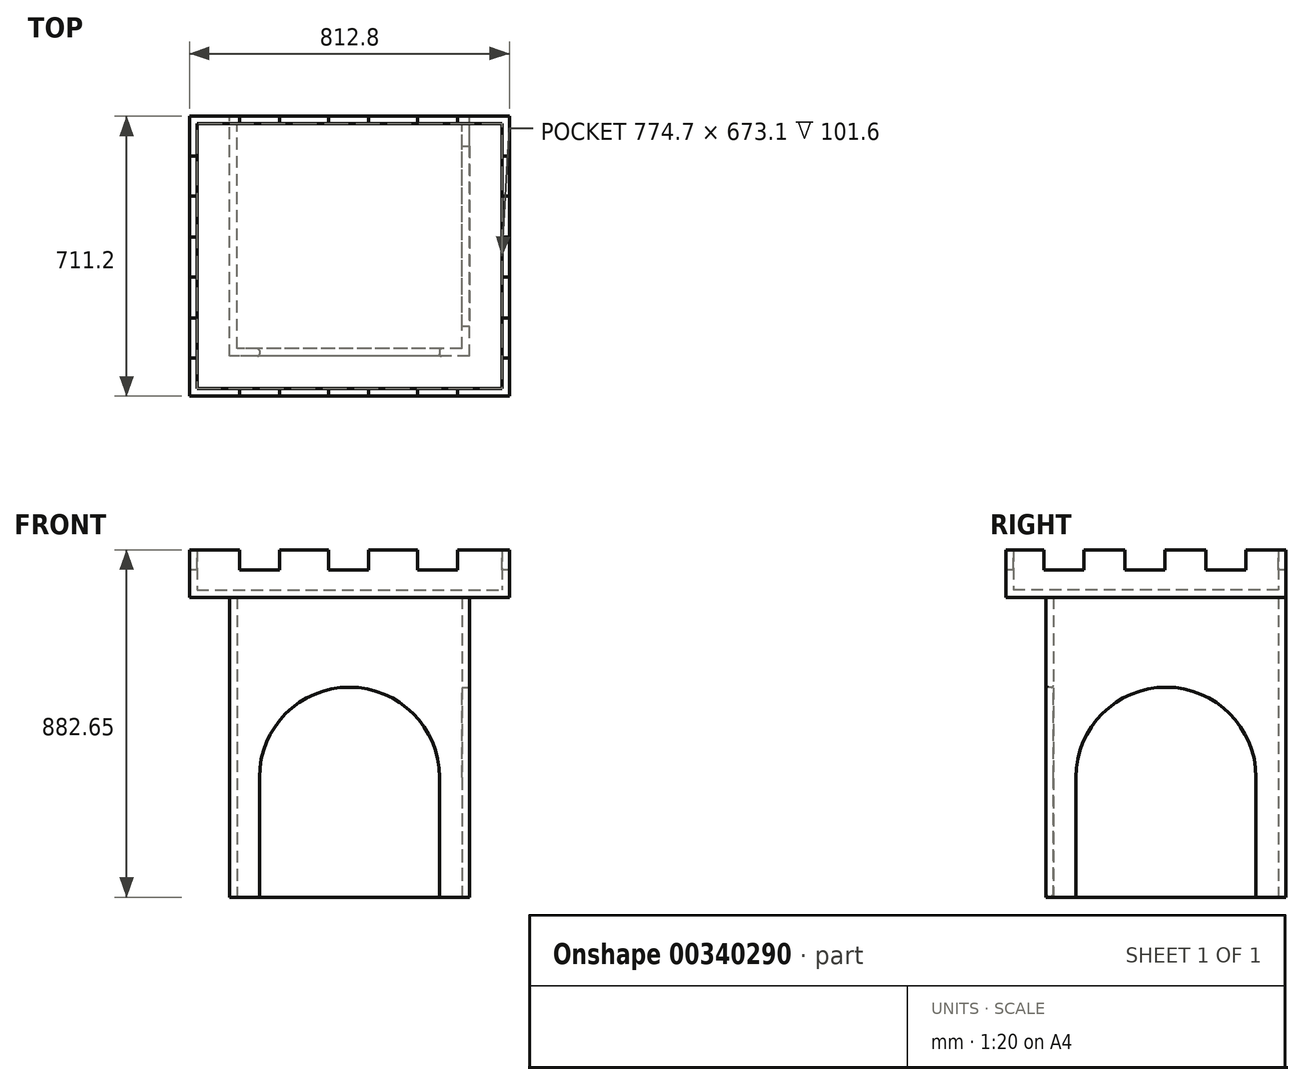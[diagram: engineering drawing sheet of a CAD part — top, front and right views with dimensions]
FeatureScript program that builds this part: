
annotation { "Feature Type Name" : "Feature", "Feature Type Description" : "" }
export const myFeature = defineFeature(function(context is Context, id is Id, definition is map)
    precondition{}
    {
        {
            var Q0;
            Q0=qCreatedBy(makeId("Top.planeOp"),FACE);
            var sketch = newSketch(context, id + "F0", { "sketchPlane" : qUnion([Q0])});
            skLineSegment(sketch, "E0.bottom", {"start": v(304.8, -304.8) * mm, "end": v(-304.8, -304.8) * mm});
            skLineSegment(sketch, "E0.top", {"start": v(304.8, 304.8) * mm, "end": v(-304.8, 304.8) * mm});
            skLineSegment(sketch, "E0.left", {"start": v(304.8, -304.8) * mm, "end": v(304.8, 304.8) * mm});
            skLineSegment(sketch, "E0.right", {"start": v(-304.8, -304.8) * mm, "end": v(-304.8, 304.8) * mm});
            skPoint(sketch, "E0.middle", {"position": v(0, 0) * mm});
            skLineSegment(sketch, "E1.bottom", {"start": v(285.75, -285.75) * mm, "end": v(-285.75, -285.75) * mm});
            skLineSegment(sketch, "E1.top", {"start": v(285.75, 285.75) * mm, "end": v(-285.75, 285.75) * mm});
            skLineSegment(sketch, "E1.left", {"start": v(285.75, -285.75) * mm, "end": v(285.75, 285.75) * mm});
            skLineSegment(sketch, "E1.right", {"start": v(-285.75, -285.75) * mm, "end": v(-285.75, 285.75) * mm});
            skSolve(sketch);
        }
        {
            var Q0;
            Q0 = qSketchRegion(id + "F0", true);
            extrude(context, id + "F1", {"entities" : qUnion([Q0]), "endBound" : BoundingType.SYMMETRIC, "depth" : 762 * mm});
        }
        {
            var Q0;
            Q0=makeQuery(id+"F1.opExtrude","SWEPT_FACE",FACE,{"disambiguationData":[OSD([sQuery(id+"F0.wireOp",EDGE,"E0.bottom")])]});
            var sketch = newSketch(context, id + "F2", { "sketchPlane" : qUnion([Q0])});
            skLineSegment(sketch, "E2.bottom", {"start": v(-228.6, -381) * mm, "end": v(228.6, -381) * mm});
            skLineSegment(sketch, "E2.top", {"start": v(-228.6, -76.2) * mm, "end": v(228.6, -76.2) * mm, "construction": true});
            skLineSegment(sketch, "E2.left", {"start": v(-228.6, -381) * mm, "end": v(-228.6, -76.2) * mm});
            skLineSegment(sketch, "E2.right", {"start": v(228.6, -381) * mm, "end": v(228.6, -76.2) * mm});
            skLineSegment(sketch, "E3", {"start": v(-304.8, -381) * mm, "end": v(-228.6, -381) * mm, "construction": true});
            skLineSegment(sketch, "E4", {"start": v(228.6, -381) * mm, "end": v(304.8, -381) * mm, "construction": true});
            skArc(sketch, "E5", {"start": v(228.6, -76.2) * mm, "mid": v(0, 152.4) * mm, "end": v(-228.6, -76.2) * mm});
            skSolve(sketch);
        }
        {
            var Q0;
            Q0 = qSketchRegion(id + "F2", true);
            extrude(context, id + "F3", {"entities" : qUnion([Q0]), "operationType" : NewBodyOperationType.REMOVE, "oppositeDirection" : true, "depth" : 25.4 * mm});
        }
        {
            var Q0;
            Q0=makeQuery(id+"F1.opExtrude","SWEPT_FACE",FACE,{"disambiguationData":[OSD([sQuery(id+"F0.wireOp",EDGE,"E0.left")])]});
            var sketch = newSketch(context, id + "F4", { "sketchPlane" : qUnion([Q0])});
            skLineSegment(sketch, "E6.bottom", {"start": v(-228.6, -381) * mm, "end": v(228.6, -381) * mm});
            skLineSegment(sketch, "E6.top", {"start": v(-228.6, -76.2) * mm, "end": v(228.6, -76.2) * mm, "construction": true});
            skLineSegment(sketch, "E6.left", {"start": v(-228.6, -381) * mm, "end": v(-228.6, -76.2) * mm});
            skLineSegment(sketch, "E6.right", {"start": v(228.6, -381) * mm, "end": v(228.6, -76.2) * mm});
            skLineSegment(sketch, "E7", {"start": v(-228.6, -381) * mm, "end": v(-304.8, -381) * mm, "construction": true});
            skLineSegment(sketch, "E8", {"start": v(228.6, -381) * mm, "end": v(304.8, -381) * mm, "construction": true});
            skArc(sketch, "E9", {"start": v(228.6, -76.2) * mm, "mid": v(0, 152.4) * mm, "end": v(-228.6, -76.2) * mm});
            skSolve(sketch);
        }
        {
            var Q0;
            Q0 = qSketchRegion(id + "F4", true);
            extrude(context, id + "F5", {"entities" : qUnion([Q0]), "operationType" : NewBodyOperationType.REMOVE, "oppositeDirection" : true, "depth" : 25.4 * mm});
        }
        {
            var Q0;
            Q0=makeQuery(id+"F3.boolean.opBoolean","COPY",FACE,{"derivedFrom":makeQuery(id+"F3.opExtrude","SWEPT_FACE",FACE,{"disambiguationData":[OSD([sQuery(id+"F2.wireOp",EDGE,"E2.left")])]})});
            var Q1;
            Q1=makeQuery(id+"F3.boolean.opBoolean","COPY",FACE,{"derivedFrom":makeQuery(id+"F3.opExtrude","SWEPT_FACE",FACE,{"disambiguationData":[OSD([sQuery(id+"F2.wireOp",EDGE,"E5")])]})});
            var Q2;
            Q2=makeQuery(id+"F3.boolean.opBoolean","COPY",FACE,{"derivedFrom":makeQuery(id+"F3.opExtrude","SWEPT_FACE",FACE,{"disambiguationData":[OSD([sQuery(id+"F2.wireOp",EDGE,"E2.right")])]})});
            fillet(context, id + "F6", {"entities" : qUnion([Q0, Q1, Q2]), "radius" : 5.08 * mm, "tangentPropagation" : true, "allowEdgeOverflow" : false});
        }
        {
            var Q0;
            Q0=makeQuery(id+"F1.opExtrude","CAP_FACE",FACE,{"disambiguationData":[OSD([sQuery(id+"F0.wireOp",EDGE,"E0.bottom"),sQuery(id+"F0.wireOp",EDGE,"E0.top"),sQuery(id+"F0.wireOp",EDGE,"E0.left"),sQuery(id+"F0.wireOp",EDGE,"E0.right"),sQuery(id+"F0.wireOp",EDGE,"E1.bottom"),sQuery(id+"F0.wireOp",EDGE,"E1.top"),sQuery(id+"F0.wireOp",EDGE,"E1.left"),sQuery(id+"F0.wireOp",EDGE,"E1.right")])],"isStart":false});
            var sketch = newSketch(context, id + "F7", { "sketchPlane" : qUnion([Q0])});
            skLineSegment(sketch, "E10.bottom", {"start": v(-406.4, 304.8) * mm, "end": v(406.4, 304.8) * mm});
            skLineSegment(sketch, "E10.top", {"start": v(-406.4, -406.4) * mm, "end": v(406.4, -406.4) * mm});
            skLineSegment(sketch, "E10.left", {"start": v(-406.4, 304.8) * mm, "end": v(-406.4, -406.4) * mm});
            skLineSegment(sketch, "E10.right", {"start": v(406.4, 304.8) * mm, "end": v(406.4, -406.4) * mm});
            skPoint(sketch, "E11", {"position": v(0, 304.8) * mm});
            skSolve(sketch);
        }
        {
            var Q0;
            Q0 = qSketchRegion(id + "F7", true);
            extrude(context, id + "F8", {"entities" : qUnion([Q0]), "operationType" : NewBodyOperationType.ADD, "depth" : 19.05 * mm});
        }
        {
            var Q0;
            Q0=makeQuery(id+"F8.opExtrude","CAP_FACE",FACE,{"disambiguationData":[OSD([sQuery(id+"F7.wireOp",EDGE,"E10.bottom"),sQuery(id+"F7.wireOp",EDGE,"E10.top"),sQuery(id+"F7.wireOp",EDGE,"E10.left"),sQuery(id+"F7.wireOp",EDGE,"E10.right")])],"isStart":false});
            var sketch = newSketch(context, id + "F9", { "sketchPlane" : qUnion([Q0])});
            skLineSegment(sketch, "E12.bottom", {"start": v(-406.4, 304.8) * mm, "end": v(406.4, 304.8) * mm});
            skLineSegment(sketch, "E12.top", {"start": v(-406.4, -406.4) * mm, "end": v(406.4, -406.4) * mm});
            skLineSegment(sketch, "E12.left", {"start": v(-406.4, 304.8) * mm, "end": v(-406.4, -406.4) * mm});
            skLineSegment(sketch, "E12.right", {"start": v(406.4, 304.8) * mm, "end": v(406.4, -406.4) * mm});
            skLineSegment(sketch, "E13.bottom", {"start": v(-387.35, 285.75) * mm, "end": v(387.35, 285.75) * mm});
            skLineSegment(sketch, "E13.top", {"start": v(-387.35, -387.35) * mm, "end": v(387.35, -387.35) * mm});
            skLineSegment(sketch, "E13.left", {"start": v(-387.35, 285.75) * mm, "end": v(-387.35, -387.35) * mm});
            skLineSegment(sketch, "E13.right", {"start": v(387.35, 285.75) * mm, "end": v(387.35, -387.35) * mm});
            skSolve(sketch);
        }
        {
            var Q0;
            Q0 = qSketchRegion(id + "F9", true);
            extrude(context, id + "F10", {"entities" : qUnion([Q0]), "operationType" : NewBodyOperationType.ADD, "depth" : 101.6 * mm});
        }
        {
            var Q0;
            Q0=makeQuery(id+"F10.boolean.opBoolean","MERGE",FACE,{"derivedFrom":[makeQuery(id+"F8.opExtrude","SWEPT_FACE",FACE,{"disambiguationData":[OSD([sQuery(id+"F7.wireOp",EDGE,"E10.top")])]}),makeQuery(id+"F10.opExtrude","SWEPT_FACE",FACE,{"disambiguationData":[OSD([sQuery(id+"F9.wireOp",EDGE,"E12.top")])]})]});
            var sketch = newSketch(context, id + "F11", { "sketchPlane" : qUnion([Q0])});
            skLineSegment(sketch, "E14", {"start": v(-406.4, 501.65) * mm, "end": v(-279.4, 501.65) * mm, "construction": true});
            skLineSegment(sketch, "E15.bottom", {"start": v(-279.4, 501.65) * mm, "end": v(-177.8, 501.65) * mm});
            skLineSegment(sketch, "E15.top", {"start": v(-279.4, 450.85) * mm, "end": v(-177.8, 450.85) * mm});
            skLineSegment(sketch, "E15.left", {"start": v(-279.4, 501.65) * mm, "end": v(-279.4, 450.85) * mm});
            skLineSegment(sketch, "E15.right", {"start": v(-177.8, 501.65) * mm, "end": v(-177.8, 450.85) * mm});
            skLineSegment(sketch, "E16.1.0.0", {"start": v(-180.34, 501.65) * mm, "end": v(-53.34, 501.65) * mm, "construction": true});
            skLineSegment(sketch, "E16.1.0.1", {"start": v(-53.34, 501.65) * mm, "end": v(48.26, 501.65) * mm});
            skLineSegment(sketch, "E16.1.0.2", {"start": v(-53.34, 450.85) * mm, "end": v(48.26, 450.85) * mm});
            skLineSegment(sketch, "E16.1.0.3", {"start": v(-53.34, 501.65) * mm, "end": v(-53.34, 450.85) * mm});
            skLineSegment(sketch, "E16.1.0.4", {"start": v(48.26, 501.65) * mm, "end": v(48.26, 450.85) * mm});
            skLineSegment(sketch, "E16.2.0.0", {"start": v(45.72, 501.65) * mm, "end": v(172.72, 501.65) * mm, "construction": true});
            skLineSegment(sketch, "E16.2.0.1", {"start": v(172.72, 501.65) * mm, "end": v(274.32, 501.65) * mm});
            skLineSegment(sketch, "E16.2.0.2", {"start": v(172.72, 450.85) * mm, "end": v(274.32, 450.85) * mm});
            skLineSegment(sketch, "E16.2.0.3", {"start": v(172.72, 501.65) * mm, "end": v(172.72, 450.85) * mm});
            skLineSegment(sketch, "E16.2.0.4", {"start": v(274.32, 501.65) * mm, "end": v(274.32, 450.85) * mm});
            skLineSegment(sketch, "E16.direction1", {"start": v(-406.4, 501.65) * mm, "end": v(-180.34, 501.65) * mm, "construction": true});
            skSolve(sketch);
        }
        {
            var Q0;
            Q0 = qSketchRegion(id + "F11", true);
            extrude(context, id + "F12", {"entities" : qUnion([Q0]), "operationType" : NewBodyOperationType.REMOVE, "endBound" : BoundingType.THROUGH_ALL, "oppositeDirection" : true, "depth" : 25.4 * mm});
        }
        {
            var Q0;
            Q0=makeQuery(id+"F10.boolean.opBoolean","MERGE",FACE,{"derivedFrom":[makeQuery(id+"F8.opExtrude","SWEPT_FACE",FACE,{"disambiguationData":[OSD([sQuery(id+"F7.wireOp",EDGE,"E10.left")])]}),makeQuery(id+"F10.opExtrude","SWEPT_FACE",FACE,{"disambiguationData":[OSD([sQuery(id+"F9.wireOp",EDGE,"E12.left")])]})]});
            var sketch = newSketch(context, id + "F13", { "sketchPlane" : qUnion([Q0])});
            skLineSegment(sketch, "E17", {"start": v(-304.8, 501.65) * mm, "end": v(-203.2, 501.65) * mm, "construction": true});
            skLineSegment(sketch, "E18.bottom", {"start": v(-203.2, 501.65) * mm, "end": v(-101.6, 501.65) * mm});
            skLineSegment(sketch, "E18.top", {"start": v(-203.2, 450.85) * mm, "end": v(-101.6, 450.85) * mm});
            skLineSegment(sketch, "E18.left", {"start": v(-203.2, 501.65) * mm, "end": v(-203.2, 450.85) * mm});
            skLineSegment(sketch, "E18.right", {"start": v(-101.6, 501.65) * mm, "end": v(-101.6, 450.85) * mm});
            skLineSegment(sketch, "E19.1.0.0", {"start": v(-99.06, 501.65) * mm, "end": v(2.54, 501.65) * mm, "construction": true});
            skLineSegment(sketch, "E19.1.0.1", {"start": v(2.54, 501.65) * mm, "end": v(104.14, 501.65) * mm});
            skLineSegment(sketch, "E19.1.0.2", {"start": v(2.54, 450.85) * mm, "end": v(104.14, 450.85) * mm});
            skLineSegment(sketch, "E19.1.0.3", {"start": v(2.54, 501.65) * mm, "end": v(2.54, 450.85) * mm});
            skLineSegment(sketch, "E19.1.0.4", {"start": v(104.14, 501.65) * mm, "end": v(104.14, 450.85) * mm});
            skLineSegment(sketch, "E19.2.0.0", {"start": v(106.68, 501.65) * mm, "end": v(208.28, 501.65) * mm, "construction": true});
            skLineSegment(sketch, "E19.2.0.1", {"start": v(208.28, 501.65) * mm, "end": v(309.88, 501.65) * mm});
            skLineSegment(sketch, "E19.2.0.2", {"start": v(208.28, 450.85) * mm, "end": v(309.88, 450.85) * mm});
            skLineSegment(sketch, "E19.2.0.3", {"start": v(208.28, 501.65) * mm, "end": v(208.28, 450.85) * mm});
            skLineSegment(sketch, "E19.2.0.4", {"start": v(309.88, 501.65) * mm, "end": v(309.88, 450.85) * mm});
            skLineSegment(sketch, "E19.direction1", {"start": v(-304.8, 501.65) * mm, "end": v(-99.06, 501.65) * mm, "construction": true});
            skSolve(sketch);
        }
        {
            var Q0;
            Q0 = qSketchRegion(id + "F13", true);
            extrude(context, id + "F14", {"entities" : qUnion([Q0]), "operationType" : NewBodyOperationType.REMOVE, "endBound" : BoundingType.THROUGH_ALL, "oppositeDirection" : true, "depth" : 25.4 * mm});
        }
    });
